# Revit family: test-Double-Panel
name_source: partatom
category: Doors
revit_build: Autodesk Revit 2015 (Build: 20140905_0730(x64)
units: mm (PartAtom-declared; Revit-internal decimal feet)

## types (18) — shared parameters
Analytic Construction = Metal
Assembly Code = C1020
Construction Type Id = MDOOR
Door Material = Door - Panel
Frame Material = Door - Frame
Function = Interior
Heat Transfer Coefficient (U) = 0.6520 BTU/(h·ft²·°F)
Rail Width-Center = 0' - 4"
Thermal Resistance (R) = 1.5338 (h·ft²·°F)/BTU
Thickness = 0' - 2"
Top Panel = 3' - 0"
Wall Closure = By host
zero-valued in all types: Solar Heat Gain Coefficient, Visual Light Transmittance

## per-type parameters (varying)
| type | Height | Width | Width Single Door |
| 72" x 82" | 6' - 10" | 6' - 0" | 3' - 0" |
| 68" x 80" | 6' - 8" | 5' - 8" | 2' - 10" |
| 72" x 84" | 7' - 0" | 6' - 0" | 3' - 0" |
| 68" x 84" | 7' - 0" | 5' - 8" | 2' - 10" |
| 38" x 96" | 8' - 0" | 3' - 2" | 1' - 7" |
| 72" x 96" | 8' - 0" | 6' - 0" | 3' - 0" |
| 42" x 96" | 8' - 0" | 3' - 6" | 1' - 9" |
| 48" x 96" | 8' - 0" | 4' - 0" | 2' - 0" |
| 60" x 84" | 7' - 0" | 5' - 0" | 2' - 6" |
| 42" x 84" | 7' - 0" | 3' - 6" | 1' - 9" |
| 44" x 84" Gas Meter | 7' - 0" | 3' - 8" | 1' - 10" |
| 48" x 60" | 5' - 0" | 4' - 0" | 2' - 0" |
| 44" x 84" | 7' - 0" | 3' - 8" | 1' - 10" |
| 60" x 96" | 8' - 0" | 5' - 0" | 2' - 6" |
| 40" x 96" | 8' - 0" | 3' - 4" | 1' - 8" |
| 44" x 96" | 8' - 0" | 3' - 8" | 1' - 10" |
| 72" x96" | 8' - 0" | 6' - 0" | 3' - 0" |
| 48" x 84" | 7' - 0" | 4' - 0" | 2' - 0" |

## geometry (parser evidence)
native form markers: Blend x4
no freeform markers — native parametric forms only
